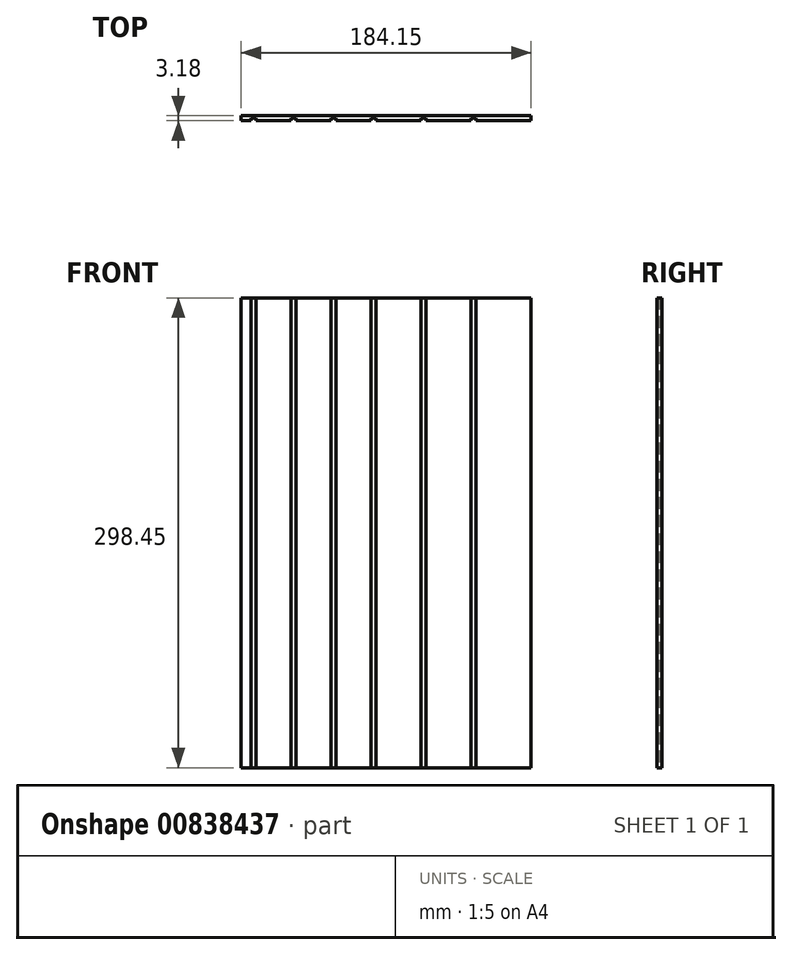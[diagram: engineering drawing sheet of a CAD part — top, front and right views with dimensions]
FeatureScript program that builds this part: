
annotation { "Feature Type Name" : "Feature", "Feature Type Description" : "" }
export const myFeature = defineFeature(function(context is Context, id is Id, definition is map)
    precondition{}
    {
        {
            var Q0;
            Q0=qCreatedBy(makeId("Top.planeOp"),FACE);
            var sketch = newSketch(context, id + "F0", { "sketchPlane" : qUnion([Q0])});
            skLineSegment(sketch, "E0.bottom", {"start": v(0, 0) * mm, "end": v(184.15, 0) * mm});
            skLineSegment(sketch, "E0.top", {"start": v(0, 298.45) * mm, "end": v(184.15, 298.45) * mm});
            skLineSegment(sketch, "E0.left", {"start": v(0, 0) * mm, "end": v(0, 298.45) * mm});
            skLineSegment(sketch, "E0.right", {"start": v(184.15, 0) * mm, "end": v(184.15, 298.45) * mm});
            skSolve(sketch);
        }
        {
            var Q0;
            Q0=makeQuery(id+"F0.imprint","IMPRINT",FACE,{"disambiguationData":[TD([[makeQuery(id+"F0.imprint","IMPRINT",EDGE,{"derivedFrom":sQuery(id+"F0.wireOp",EDGE,"E0.bottom")}),1.0]])]});
            extrude(context, id + "F1", {"entities" : qUnion([Q0]), "depth" : 3.17 * mm, "offsetDistance" : 25.4 * mm});
        }
        {
            var Q0;
            Q0=makeQuery(id+"F1.opExtrude","CAP_FACE",FACE,{"disambiguationData":[OSD([sQuery(id+"F0.wireOp",EDGE,"E0.bottom"),sQuery(id+"F0.wireOp",EDGE,"E0.top"),sQuery(id+"F0.wireOp",EDGE,"E0.left"),sQuery(id+"F0.wireOp",EDGE,"E0.right")])],"isStart":false});
            var sketch = newSketch(context, id + "F2", { "sketchPlane" : qUnion([Q0])});
            skLineSegment(sketch, "E1.bottom", {"start": v(149.22, 298.45) * mm, "end": v(146.05, 298.45) * mm});
            skLineSegment(sketch, "E1.top", {"start": v(149.22, 0) * mm, "end": v(146.05, 0) * mm});
            skLineSegment(sketch, "E1.left", {"start": v(149.22, 298.45) * mm, "end": v(149.22, 0) * mm});
            skLineSegment(sketch, "E1.right", {"start": v(146.05, 298.45) * mm, "end": v(146.05, 0) * mm});
            skLineSegment(sketch, "E2.bottom", {"start": v(117.47, 298.45) * mm, "end": v(114.3, 298.45) * mm});
            skLineSegment(sketch, "E2.top", {"start": v(117.47, 0) * mm, "end": v(114.3, 0) * mm});
            skLineSegment(sketch, "E2.left", {"start": v(117.47, 298.45) * mm, "end": v(117.47, 0) * mm});
            skLineSegment(sketch, "E2.right", {"start": v(114.3, 298.45) * mm, "end": v(114.3, 0) * mm});
            skLineSegment(sketch, "E3.bottom", {"start": v(85.72, 0) * mm, "end": v(82.55, 0) * mm});
            skLineSegment(sketch, "E3.top", {"start": v(85.72, 298.45) * mm, "end": v(82.55, 298.45) * mm});
            skLineSegment(sketch, "E3.left", {"start": v(85.72, 0) * mm, "end": v(85.72, 298.45) * mm});
            skLineSegment(sketch, "E3.right", {"start": v(82.55, 0) * mm, "end": v(82.55, 298.45) * mm});
            skLineSegment(sketch, "E4.bottom", {"start": v(34.92, 0) * mm, "end": v(31.75, 0) * mm});
            skLineSegment(sketch, "E4.top", {"start": v(34.92, 298.45) * mm, "end": v(31.75, 298.45) * mm});
            skLineSegment(sketch, "E4.left", {"start": v(34.92, 0) * mm, "end": v(34.92, 298.45) * mm});
            skLineSegment(sketch, "E4.right", {"start": v(31.75, 0) * mm, "end": v(31.75, 298.45) * mm});
            skLineSegment(sketch, "E5.bottom", {"start": v(57.15, 0) * mm, "end": v(60.32, 0) * mm});
            skLineSegment(sketch, "E5.top", {"start": v(57.15, 298.45) * mm, "end": v(60.32, 298.45) * mm});
            skLineSegment(sketch, "E5.left", {"start": v(57.15, 0) * mm, "end": v(57.15, 298.45) * mm});
            skLineSegment(sketch, "E5.right", {"start": v(60.32, 0) * mm, "end": v(60.32, 298.45) * mm});
            skLineSegment(sketch, "E6.bottom", {"start": v(9.52, 0) * mm, "end": v(6.35, 0) * mm});
            skLineSegment(sketch, "E6.top", {"start": v(9.52, 298.45) * mm, "end": v(6.35, 298.45) * mm});
            skLineSegment(sketch, "E6.left", {"start": v(9.52, 0) * mm, "end": v(9.52, 298.45) * mm});
            skLineSegment(sketch, "E6.right", {"start": v(6.35, 0) * mm, "end": v(6.35, 298.45) * mm});
            skSolve(sketch);
        }
        {
            var Q0;
            Q0=makeQuery(id+"F2.imprint","IMPRINT",FACE,{"disambiguationData":[TD([[makeQuery(id+"F2.imprint","IMPRINT",EDGE,{"derivedFrom":sQuery(id+"F2.wireOp",EDGE,"E6.bottom")}),1.0]])]});
            var Q1;
            Q1=makeQuery(id+"F2.imprint","IMPRINT",FACE,{"disambiguationData":[TD([[makeQuery(id+"F2.imprint","IMPRINT",EDGE,{"derivedFrom":sQuery(id+"F2.wireOp",EDGE,"E4.bottom")}),1.0]])]});
            var Q2;
            Q2=makeQuery(id+"F2.imprint","IMPRINT",FACE,{"disambiguationData":[TD([[makeQuery(id+"F2.imprint","IMPRINT",EDGE,{"derivedFrom":sQuery(id+"F2.wireOp",EDGE,"E5.bottom")}),1.0]])]});
            var Q3;
            Q3=makeQuery(id+"F2.imprint","IMPRINT",FACE,{"disambiguationData":[TD([[makeQuery(id+"F2.imprint","IMPRINT",EDGE,{"derivedFrom":sQuery(id+"F2.wireOp",EDGE,"E3.bottom")}),1.0]])]});
            var Q4;
            Q4=makeQuery(id+"F2.imprint","IMPRINT",FACE,{"disambiguationData":[TD([[makeQuery(id+"F2.imprint","IMPRINT",EDGE,{"derivedFrom":sQuery(id+"F2.wireOp",EDGE,"E2.bottom")}),-1.0]])]});
            var Q5;
            Q5=makeQuery(id+"F2.imprint","IMPRINT",FACE,{"disambiguationData":[TD([[makeQuery(id+"F2.imprint","IMPRINT",EDGE,{"derivedFrom":sQuery(id+"F2.wireOp",EDGE,"E1.bottom")}),-1.0]])]});
            extrude(context, id + "F3", {"entities" : qUnion([Q0, Q1, Q2, Q3, Q4, Q5]), "operationType" : NewBodyOperationType.REMOVE, "oppositeDirection" : true, "depth" : 1.59 * mm, "offsetDistance" : 25.4 * mm});
        }
        {
            var Q0;
            Q0=makeQuery(id+"F1.opExtrude","SWEPT_BODY",BODY,{"disambiguationData":[OSD([sQuery(id+"F0.wireOp",EDGE,"E0.bottom"),sQuery(id+"F0.wireOp",EDGE,"E0.top"),sQuery(id+"F0.wireOp",EDGE,"E0.left"),sQuery(id+"F0.wireOp",EDGE,"E0.right")])]});
            var Q1;
            Q1=makeQuery(id+"F1.opExtrude","CAP_EDGE",EDGE,{"disambiguationData":[OSD([sQuery(id+"F0.wireOp",EDGE,"E0.bottom")])],"isStart":true});
            transform(context, id + "F4", {"entities" : qUnion([Q0]), "transformType" : TransformType.ROTATION, "transformAxis" : qUnion([Q1]), "angle" : 90 * degree, "makeCopy" : false});
        }
    });
